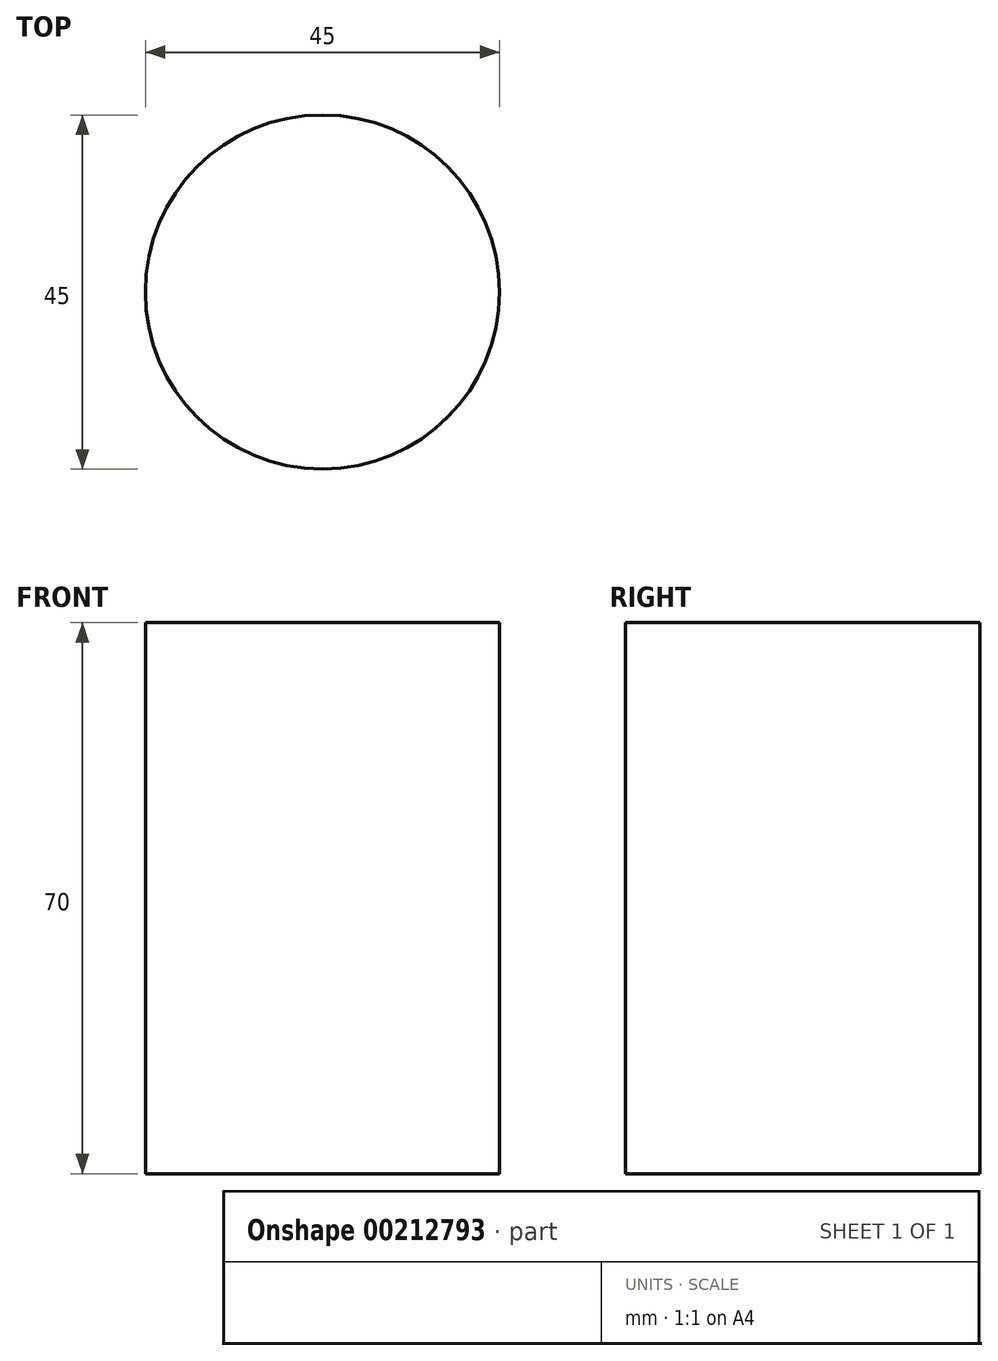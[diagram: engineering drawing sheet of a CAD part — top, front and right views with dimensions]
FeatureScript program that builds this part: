
annotation { "Feature Type Name" : "Feature", "Feature Type Description" : "" }
export const myFeature = defineFeature(function(context is Context, id is Id, definition is map)
    precondition{}
    {
        {
            var Q0;
            Q0=qCreatedBy(makeId("Top.planeOp"),FACE);
            var sketch = newSketch(context, id + "F0", { "sketchPlane" : qUnion([Q0])});
            skCircle(sketch, "E0", {"center": v(0, 0) * mm, "radius": 22.5 * mm});
            skSolve(sketch);
        }
        {
            var Q0;
            Q0=makeQuery(id+"F0.imprint","IMPRINT",FACE,{"disambiguationData":[TD([[makeQuery(id+"F0.imprint","IMPRINT",EDGE,{"derivedFrom":sQuery(id+"F0.wireOp",EDGE,"E0")}),1.0]])]});
            extrude(context, id + "F1", {"entities" : qUnion([Q0]), "depth" : 70 * mm});
        }
    });
